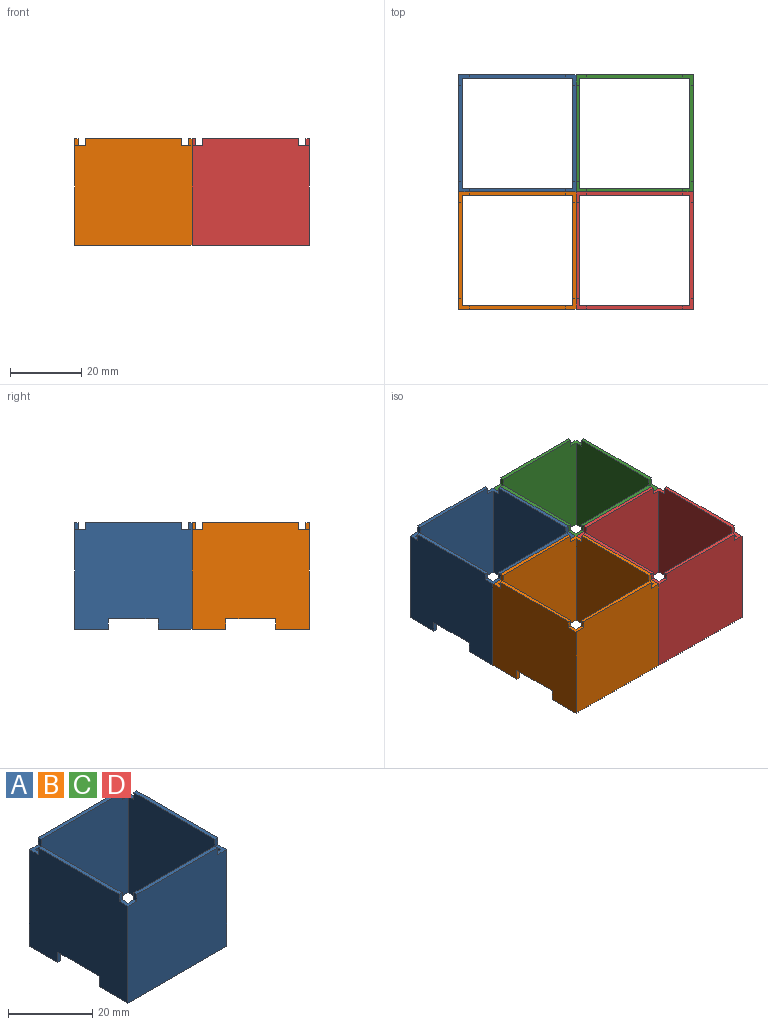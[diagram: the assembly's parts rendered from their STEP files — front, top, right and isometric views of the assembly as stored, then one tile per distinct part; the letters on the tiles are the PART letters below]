
ASSEMBLY  parts=4 mates=3
PART A: 32 faces, bbox 33x33x30 mm
  f0: plane 33x30mm, normal (-1,0,0), area 936mm2, adj f2,f3,f4,f11,f13,f17,f18,f19
  f1: plane 33x30mm, normal (1,0,0), area 936mm2, adj f2,f3,f6,f11,f13,f14,f15,f16
  f2: plane 33x30mm, normal (0,1,0), area 978mm2, adj f0,f1,f11,f12,f27,f28,f30,f31
  f3: plane 33x30mm, normal (0,-1,0), area 978mm2, adj f0,f1,f5,f13,f21,f22,f24,f25
  f4: plane 27x1mm, normal (0,0,1), area 27mm2, adj f0,f7,f23,f26
  f5: plane 27x1mm, normal (0,0,1), area 27mm2, adj f3,f10,f21,f24
  f6: plane 27x1mm, normal (0,0,1), area 27mm2, adj f1,f8,f20,f29
  f7: plane 31x30mm, normal (1,0,0), area 880mm2, adj f4,f9,f10,f11,f13,f17,f18,f19
  f8: plane 31x30mm, normal (-1,0,0), area 880mm2, adj f6,f9,f10,f11,f13,f14,f15,f16
  f9: plane 31x30mm, normal (0,-1,0), area 922mm2, adj f7,f8,f11,f12,f27,f28,f30,f31
  f10: plane 31x30mm, normal (0,1,0), area 922mm2, adj f5,f7,f8,f13,f21,f22,f24,f25
  f11: plane 33x9.5mm, normal (0,0,-1), area 50mm2, adj f0,f1,f2,f7,f8,f9,f15,f19
  f12: plane 27x1mm, normal (0,0,1), area 27mm2, adj f2,f9,f27,f30
  f13: plane 33x9.5mm, normal (0,0,-1), area 50mm2, adj f0,f1,f3,f7,f8,f10,f16,f18
  f14: plane 14x1mm, normal (0,0,-1), area 14mm2, adj f1,f8,f15,f16
  f15: plane 3x1mm, normal (0,-1,0), area 3mm2, adj f1,f8,f11,f14
  f16: plane 3x1mm, normal (0,1,0), area 3mm2, adj f1,f8,f13,f14
  f17: plane 14x1mm, normal (0,0,-1), area 14mm2, adj f0,f7,f18,f19
  f18: plane 3x1mm, normal (0,1,0), area 3mm2, adj f0,f7,f13,f17
  f19: plane 3x1mm, normal (0,-1,0), area 3mm2, adj f0,f7,f11,f17
  f20: plane 2x1mm, normal (0,-1,0), area 2mm2, adj f1,f6,f8,f22
  f21: plane 2x1mm, normal (1,0,0), area 2mm2, adj f3,f5,f10,f22
  f22: plane 3x3mm, normal (0,0,1), area 5mm2, adj f1,f3,f8,f10,f20,f21
  f23: plane 2x1mm, normal (0,-1,0), area 2mm2, adj f0,f4,f7,f25
  f24: plane 2x1mm, normal (-1,0,0), area 2mm2, adj f3,f5,f10,f25
  f25: plane 3x3mm, normal (0,0,1), area 5mm2, adj f0,f3,f7,f10,f23,f24
  f26: plane 2x1mm, normal (0,1,0), area 2mm2, adj f0,f4,f7,f28
  f27: plane 2x1mm, normal (-1,0,0), area 2mm2, adj f2,f9,f12,f28
  f28: plane 3x3mm, normal (0,0,1), area 5mm2, adj f0,f2,f7,f9,f26,f27
  f29: plane 2x1mm, normal (0,1,0), area 2mm2, adj f1,f6,f8,f31
  f30: plane 2x1mm, normal (1,0,0), area 2mm2, adj f2,f9,f12,f31
  f31: plane 3x3mm, normal (0,0,1), area 5mm2, adj f1,f2,f8,f9,f29,f30
PART B: same geometry as A
PART C: same geometry as A
PART D: same geometry as A
PLACE A t=(-34.45,-19.24,11.07)mm
PLACE B t=(-34.45,-52.24,11.07)mm
PLACE C t=(-1.45,-19.24,11.07)mm
PLACE D t=(-1.45,-52.24,11.07)mm
MATE fastened B.f2 <-> A.f3  axis (0,1,0) through (-55.21,-8.59,25.9)mm
MATE fastened C.f0 <-> A.f1  axis (-1,0,0) through (-38.71,7.91,26.5)mm
MATE fastened D.f0 <-> B.f1  axis (-1,0,0) through (-38.71,-25.09,26.5)mm
